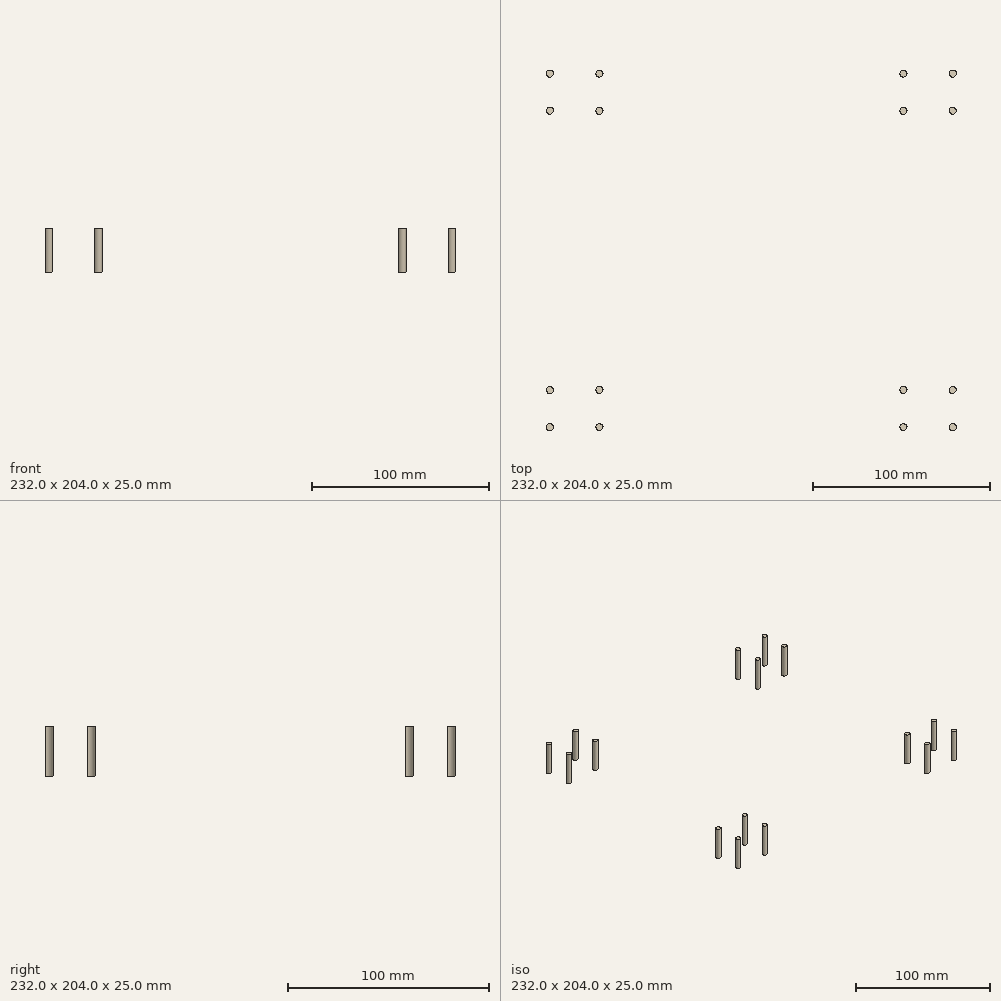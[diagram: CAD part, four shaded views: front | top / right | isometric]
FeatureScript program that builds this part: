
annotation { "Feature Type Name" : "Feature", "Feature Type Description" : "" }
export const myFeature = defineFeature(function(context is Context, id is Id, definition is map)
    precondition{}
    {
        {
            var Q0;
            Q0=qCreatedBy(makeId("Top.planeOp"),FACE);
            var sketch = newSketch(context, id + "F0", { "sketchPlane" : qUnion([Q0])});
            skLineSegment(sketch, "E0.bottom", {"start": v(0, 0) * mm, "end": v(-100, 0) * mm, "construction": true});
            skLineSegment(sketch, "E0.left", {"start": v(0, 0) * mm, "end": v(0, 100) * mm, "construction": true});
            skLineSegment(sketch, "E1.right", {"start": v(-86, 100) * mm, "end": v(-86, 100) * mm});
            skCircle(sketch, "E2", {"center": v(-86, 100) * mm, "radius": 2 * mm});
            skCircle(sketch, "E3", {"center": v(-86, 79) * mm, "radius": 2 * mm});
            skCircle(sketch, "E4.MirrorC", {"center": v(-114, 100) * mm, "radius": 2 * mm});
            skCircle(sketch, "E5.MirrorC", {"center": v(-114, 79) * mm, "radius": 2 * mm});
            skCircle(sketch, "E6.MirrorC", {"center": v(114, 100) * mm, "radius": 2 * mm});
            skCircle(sketch, "E7.MirrorC", {"center": v(114, 79) * mm, "radius": 2 * mm});
            skCircle(sketch, "E8.MirrorC", {"center": v(86, 100) * mm, "radius": 2 * mm});
            skCircle(sketch, "E9.MirrorC", {"center": v(86, 79) * mm, "radius": 2 * mm});
            skCircle(sketch, "E10.MirrorC", {"center": v(86, -79) * mm, "radius": 2 * mm});
            skCircle(sketch, "E11.MirrorC", {"center": v(86, -100) * mm, "radius": 2 * mm});
            skCircle(sketch, "E12.MirrorC", {"center": v(114, -79) * mm, "radius": 2 * mm});
            skCircle(sketch, "E13.MirrorC", {"center": v(114, -100) * mm, "radius": 2 * mm});
            skCircle(sketch, "E14.MirrorC", {"center": v(-86, -100) * mm, "radius": 2 * mm});
            skCircle(sketch, "E15.MirrorC", {"center": v(-86, -79) * mm, "radius": 2 * mm});
            skLineSegment(sketch, "E16.MirrorCS", {"start": v(-86, -100) * mm, "end": v(-86, -100) * mm});
            skCircle(sketch, "E17.MirrorC", {"center": v(-114, -100) * mm, "radius": 2 * mm});
            skCircle(sketch, "E18.MirrorC", {"center": v(-114, -79) * mm, "radius": 2 * mm});
            skSolve(sketch);
        }
        {
            var Q0;
            Q0 = qSketchRegion(id + "F0", true);
            extrude(context, id + "F1", {"entities" : qUnion([Q0]), "depth" : 25 * mm});
        }
    });
